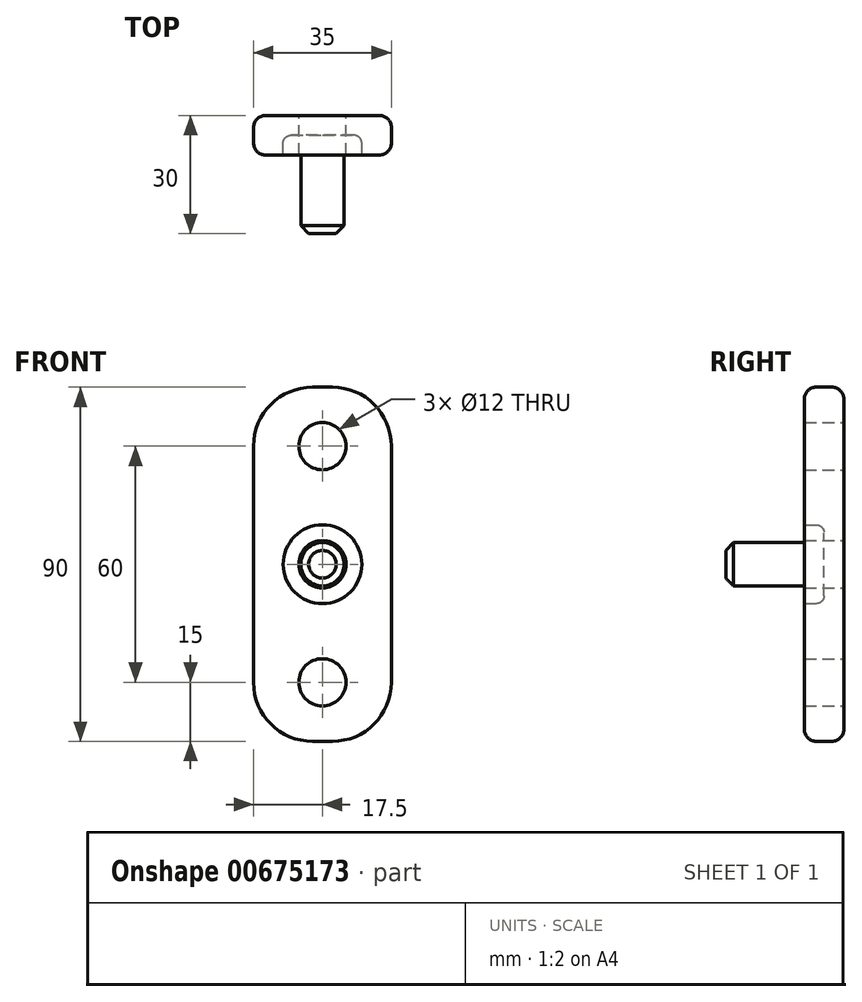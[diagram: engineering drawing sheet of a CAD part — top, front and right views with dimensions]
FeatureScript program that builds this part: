
annotation { "Feature Type Name" : "Feature", "Feature Type Description" : "" }
export const myFeature = defineFeature(function(context is Context, id is Id, definition is map)
    precondition{}
    {
        {
            var Q0;
            Q0=qCreatedBy(makeId("Front.planeOp"),FACE);
            var sketch = newSketch(context, id + "F0", { "sketchPlane" : qUnion([Q0])});
            skLineSegment(sketch, "E0.bottom", {"start": v(2.5, 45) * mm, "end": v(-2.5, 45) * mm});
            skLineSegment(sketch, "E0.top", {"start": v(2.5, -45) * mm, "end": v(-2.5, -45) * mm});
            skLineSegment(sketch, "E0.left", {"start": v(17.5, 30) * mm, "end": v(17.5, -30) * mm});
            skLineSegment(sketch, "E0.right", {"start": v(-17.5, 30) * mm, "end": v(-17.5, -30) * mm});
            skPoint(sketch, "E0.middle", {"position": v(0, 0) * mm});
            skCircle(sketch, "E1", {"center": v(0, 30) * mm, "radius": 6 * mm});
            skCircle(sketch, "E2", {"center": v(0, -30) * mm, "radius": 6 * mm});
            skCircle(sketch, "E3", {"center": v(0, 0) * mm, "radius": 6 * mm});
            skPoint(sketch, "E4.visualSharp", {"position": v(17.5, 45) * mm});
            skArc(sketch, "E4.filletArc", {"start": v(17.5, 30) * mm, "mid": v(13.1, 40.6) * mm, "end": v(2.5, 45) * mm});
            skPoint(sketch, "E5.visualSharp", {"position": v(-17.5, 45) * mm});
            skArc(sketch, "E5.filletArc", {"start": v(-2.5, 45) * mm, "mid": v(-13.1, 40.6) * mm, "end": v(-17.5, 30) * mm});
            skPoint(sketch, "E6.visualSharp", {"position": v(17.5, -45) * mm});
            skArc(sketch, "E6.filletArc", {"start": v(2.5, -45) * mm, "mid": v(13.1, -40.6) * mm, "end": v(17.5, -30) * mm});
            skPoint(sketch, "E7.visualSharp", {"position": v(-17.5, -45) * mm});
            skArc(sketch, "E7.filletArc", {"start": v(-17.5, -30) * mm, "mid": v(-13.1, -40.6) * mm, "end": v(-2.5, -45) * mm});
            skSolve(sketch);
        }
        {
            var Q0;
            Q0 = qSketchRegion(id + "F0", true);
            extrude(context, id + "F1", {"entities" : qUnion([Q0]), "endBound" : BoundingType.SYMMETRIC, "depth" : 10 * mm, "offsetDistance" : 25 * mm});
        }
        {
            var Q0;
            Q0=makeQuery(id+"F1.opExtrude","CAP_EDGE",EDGE,{"disambiguationData":[OSD([sQuery(id+"F0.wireOp",EDGE,"E0.left")])],"isStart":false});
            fillet(context, id + "F2", {"entities" : qUnion([Q0]), "radius" : 3 * mm, "tangentPropagation" : true, "allowEdgeOverflow" : false});
        }
        {
            var Q0;
            Q0=makeQuery(id+"F1.opExtrude","CAP_EDGE",EDGE,{"disambiguationData":[OSD([sQuery(id+"F0.wireOp",EDGE,"E0.left")])],"isStart":true});
            fillet(context, id + "F3", {"entities" : qUnion([Q0]), "radius" : 3 * mm, "tangentPropagation" : true, "allowEdgeOverflow" : false});
        }
        {
            var Q0;
            Q0=qCreatedBy(makeId("Front.planeOp"),FACE);
            var sketch = newSketch(context, id + "F4", { "sketchPlane" : qUnion([Q0])});
            skCircle(sketch, "E8", {"center": v(0, 0) * mm, "radius": 5.5 * mm});
            skCircle(sketch, "E9", {"center": v(0, 0) * mm, "radius": 10 * mm});
            skSolve(sketch);
        }
        {
            var Q0;
            Q0=makeQuery(id+"F4.imprint","IMPRINT",FACE,{"disambiguationData":[TD([[makeQuery(id+"F4.imprint","IMPRINT",EDGE,{"derivedFrom":sQuery(id+"F4.wireOp",EDGE,"E8")}),-1.0]])]});
            var Q1;
            Q1=sQuery(id+"F4.wireOp",EDGE,"E9");
            extrude(context, id + "F5", {"entities" : qUnion([Q0]), "surfaceEntities" : qUnion([Q1]), "depth" : 5 * mm, "offsetDistance" : 25 * mm});
        }
        {
            var Q0;
            Q0=makeQuery(id+"F4.imprint","IMPRINT",FACE,{"disambiguationData":[TD([[makeQuery(id+"F4.imprint","IMPRINT",EDGE,{"derivedFrom":sQuery(id+"F4.wireOp",EDGE,"E8")}),1.0]])]});
            extrude(context, id + "F6", {"entities" : qUnion([Q0]), "operationType" : NewBodyOperationType.ADD, "depth" : 25 * mm, "offsetDistance" : 25 * mm});
        }
        {
            var Q0;
            Q0=makeQuery(id+"F6.opExtrude","CAP_EDGE",EDGE,{"disambiguationData":[OSD([sQuery(id+"F4.wireOp",EDGE,"E8")])],"isStart":false});
            chamfer(context, id + "F7", {"entities" : qUnion([Q0]), "width" : 2 * mm, "tangentPropagation" : true});
        }
        {
            var Q0;
            Q0=makeQuery(id+"F5.opExtrude","CAP_EDGE",EDGE,{"disambiguationData":[OSD([sQuery(id+"F4.wireOp",EDGE,"E9")])],"isStart":true});
            fillet(context, id + "F8", {"entities" : qUnion([Q0]), "radius" : 2 * mm, "tangentPropagation" : true, "allowEdgeOverflow" : false});
        }
    });
